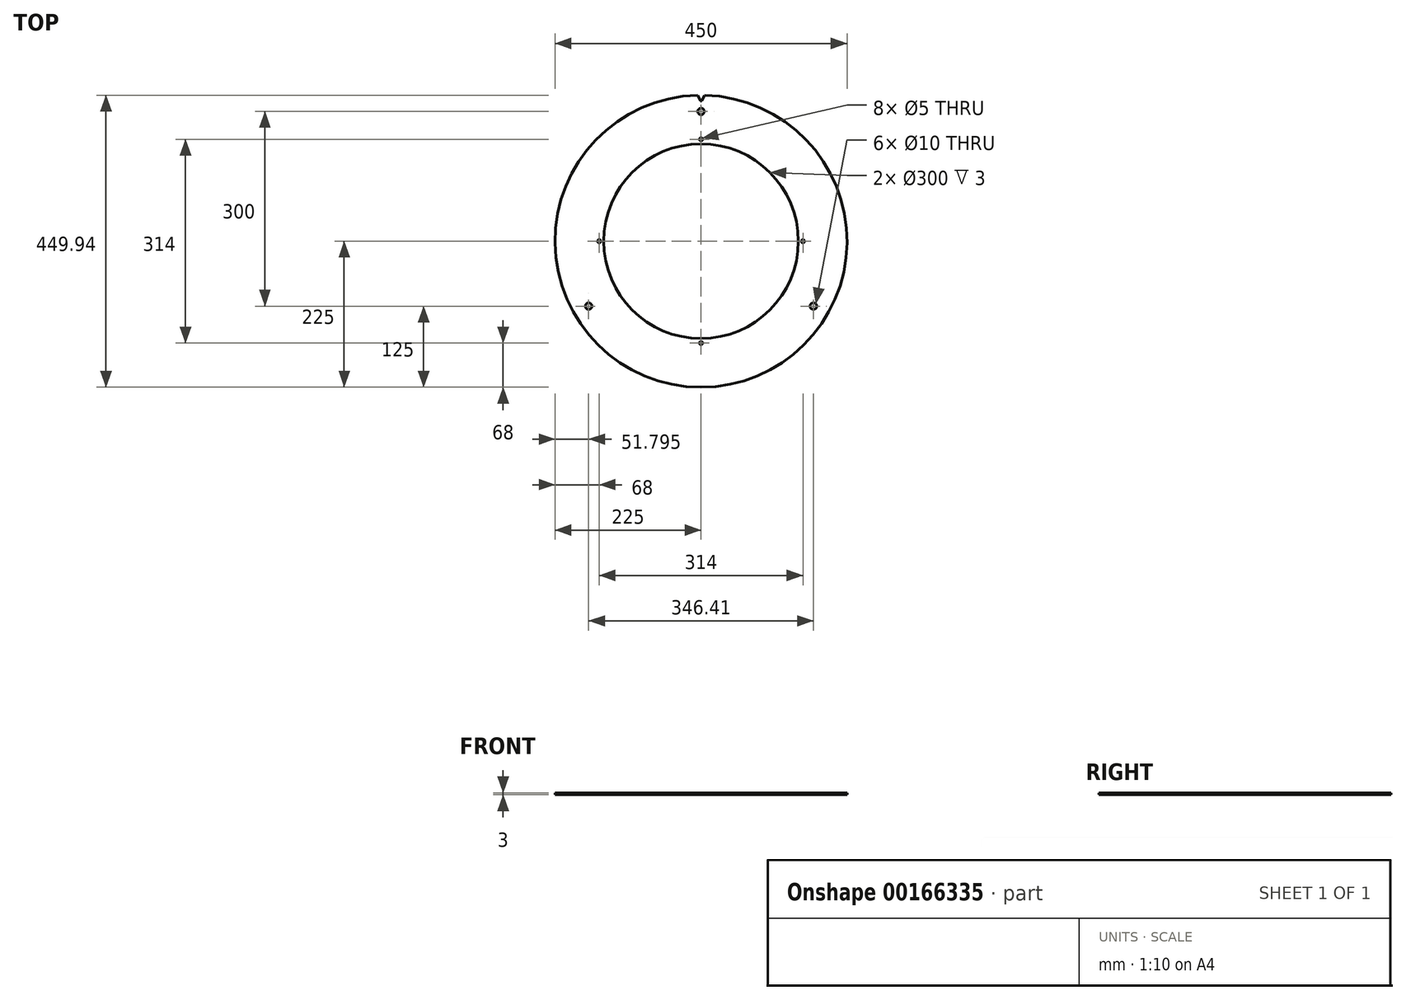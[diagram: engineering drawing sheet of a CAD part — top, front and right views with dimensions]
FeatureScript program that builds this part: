
annotation { "Feature Type Name" : "Feature", "Feature Type Description" : "" }
export const myFeature = defineFeature(function(context is Context, id is Id, definition is map)
    precondition{}
    {
        {
            var Q0;
            Q0=qCreatedBy(makeId("Top.planeOp"),FACE);
            var sketch = newSketch(context, id + "F0", { "sketchPlane" : qUnion([Q0])});
            skCircle(sketch, "E0", {"center": v(0, 0) * mm, "radius": 225 * mm});
            skCircle(sketch, "E1", {"center": v(0, 0) * mm, "radius": 150 * mm});
            skSolve(sketch);
        }
        {
            var Q0;
            Q0=makeQuery(id+"F0.imprint","IMPRINT",FACE,{"disambiguationData":[TD([[makeQuery(id+"F0.imprint","IMPRINT",EDGE,{"derivedFrom":sQuery(id+"F0.wireOp",EDGE,"E0")}),1.0]])]});
            extrude(context, id + "F1", {"entities" : qUnion([Q0]), "depth" : 3 * mm});
        }
        {
            var Q0;
            Q0=makeQuery(id+"F1.opExtrude","CAP_FACE",FACE,{"disambiguationData":[OSD([sQuery(id+"F0.wireOp",EDGE,"E0"),sQuery(id+"F0.wireOp",EDGE,"E1")])],"isStart":false});
            var sketch = newSketch(context, id + "F2", { "sketchPlane" : qUnion([Q0])});
            skLineSegment(sketch, "E2", {"start": v(0, 0) * mm, "end": v(0, 200) * mm});
            skCircle(sketch, "E3", {"center": v(0, 200) * mm, "radius": 5 * mm});
            skCircle(sketch, "E4.1.0", {"center": v(-173.2, -100) * mm, "radius": 5 * mm});
            skCircle(sketch, "E4.2.0", {"center": v(173.2, -100) * mm, "radius": 5 * mm});
            skPoint(sketch, "E4.center", {"position": v(0, 0) * mm});
            skSolve(sketch);
        }
        {
            var Q0;
            Q0=qSketchRegion(id+"F2",true);
            extrude(context, id + "F3", {"entities" : qUnion([Q0]), "operationType" : NewBodyOperationType.REMOVE, "oppositeDirection" : true, "depth" : 3 * mm});
        }
        {
            var Q0;
            Q0=makeQuery(id+"F1.opExtrude","CAP_FACE",FACE,{"disambiguationData":[OSD([sQuery(id+"F0.wireOp",EDGE,"E0"),sQuery(id+"F0.wireOp",EDGE,"E1")])],"isStart":false});
            var sketch = newSketch(context, id + "F4", { "sketchPlane" : qUnion([Q0])});
            skLineSegment(sketch, "E5", {"start": v(0, 0) * mm, "end": v(0, 157) * mm});
            skCircle(sketch, "E6", {"center": v(0, 157) * mm, "radius": 2.5 * mm});
            skCircle(sketch, "E7.1.0", {"center": v(-157, 0) * mm, "radius": 2.5 * mm});
            skCircle(sketch, "E7.2.0", {"center": v(0, -157) * mm, "radius": 2.5 * mm});
            skCircle(sketch, "E7.3.0", {"center": v(157, 0) * mm, "radius": 2.5 * mm});
            skPoint(sketch, "E7.center", {"position": v(0, 0) * mm});
            skSolve(sketch);
        }
        {
            var Q0;
            Q0=qSketchRegion(id+"F4",true);
            extrude(context, id + "F5", {"entities" : qUnion([Q0]), "operationType" : NewBodyOperationType.REMOVE, "oppositeDirection" : true, "depth" : 3 * mm});
        }
        {
            var Q0;
            Q0=makeQuery(id+"F1.opExtrude","CAP_FACE",FACE,{"disambiguationData":[OSD([sQuery(id+"F0.wireOp",EDGE,"E0"),sQuery(id+"F0.wireOp",EDGE,"E1")])],"isStart":false});
            var sketch = newSketch(context, id + "F6", { "sketchPlane" : qUnion([Q0])});
            skLineSegment(sketch, "E8", {"start": v(0, 0) * mm, "end": v(0, 216.45) * mm});
            skCircle(sketch, "E9", {"center": v(0, 216.45) * mm, "radius": 0.55 * mm});
            skLineSegment(sketch, "E10", {"start": v(0, 0) * mm, "end": v(-2, 216.44) * mm});
            skLineSegment(sketch, "E11", {"start": v(0, 0) * mm, "end": v(2, 216.44) * mm});
            skLineSegment(sketch, "E12", {"start": v(0, 216.45) * mm, "end": v(-2, 216.44) * mm});
            skLineSegment(sketch, "E13", {"start": v(0, 216.45) * mm, "end": v(2, 216.44) * mm});
            skLineSegment(sketch, "E14", {"start": v(-1, 216.45) * mm, "end": v(-7.36, 228.95) * mm});
            skLineSegment(sketch, "E15", {"start": v(-7.36, 228.95) * mm, "end": v(6.62, 227.33) * mm});
            skLineSegment(sketch, "E16", {"start": v(6.62, 227.33) * mm, "end": v(1, 216.45) * mm});
            skSolve(sketch);
        }
        {
            var Q0;
            {var subQ1=sQuery(id+"F6.wireOp",EDGE,"E12");var subQ9=sQuery(id+"F6.wireOp",EDGE,"E9");var subQ11=makeQuery(id+"F6.imprint","INTERSECT",VERTEX,{"derivedFrom":[subQ9,subQ1]});Q0=makeQuery(id+"F6.imprint","IMPRINT",FACE,{"disambiguationData":[TD([[makeQuery(id+"F6.imprint","IMPRINT",EDGE,{"disambiguationData":[TD([[subQ11,1.0]])],"derivedFrom":subQ9}),-1.0]])]});}
            var Q1;
            {var subQ0=sQuery(id+"F6.wireOp",EDGE,"E12");var subQ1=sQuery(id+"F6.wireOp",EDGE,"E9");var subQ2=makeQuery(id+"F6.imprint","INTERSECT",VERTEX,{"derivedFrom":[subQ1,subQ0]});Q1=makeQuery(id+"F6.imprint","IMPRINT",FACE,{"disambiguationData":[TD([[makeQuery(id+"F6.imprint","IMPRINT",EDGE,{"disambiguationData":[TD([[subQ2,1.0]])],"derivedFrom":subQ1}),1.0]])]});}
            var Q2;
            {var subQ1=sQuery(id+"F6.wireOp",EDGE,"E8");var subQ3=sQuery(id+"F6.wireOp",EDGE,"E9");var subQ4=makeQuery(id+"F6.imprint","INTERSECT",VERTEX,{"derivedFrom":[subQ1,subQ3]});Q2=makeQuery(id+"F6.imprint","IMPRINT",FACE,{"disambiguationData":[TD([[makeQuery(id+"F6.imprint","IMPRINT",EDGE,{"disambiguationData":[TD([[subQ4,-1.0]])],"derivedFrom":subQ3}),1.0]])]});}
            var Q3;
            {var subQ1=sQuery(id+"F6.wireOp",EDGE,"E8");var subQ3=sQuery(id+"F6.wireOp",EDGE,"E9");var subQ4=makeQuery(id+"F6.imprint","INTERSECT",VERTEX,{"derivedFrom":[subQ1,subQ3]});Q3=makeQuery(id+"F6.imprint","IMPRINT",FACE,{"disambiguationData":[TD([[makeQuery(id+"F6.imprint","IMPRINT",EDGE,{"disambiguationData":[TD([[subQ4,1.0]])],"derivedFrom":subQ3}),1.0]])]});}
            extrude(context, id + "F7", {"entities" : qUnion([Q0, Q1, Q2, Q3]), "operationType" : NewBodyOperationType.REMOVE, "oppositeDirection" : true, "depth" : 25 * mm});
        }
    });
